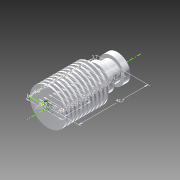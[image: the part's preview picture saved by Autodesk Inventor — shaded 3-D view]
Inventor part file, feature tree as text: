
AUTODESK INVENTOR PART (.ipt)
format: ipt  version: 2015 (Build 190159000, 159)  size: 478,720 bytes
history: native  units: mm
features: sketch x3, hole x3, other x2, revolve x1
ambient origin geometry x8: Origin, YZ Plane, XZ Plane, XY Plane, X Axis, Y Axis, Z Axis, Center Point
bodies: Body1 (feature_tree)
feature tree (9):
  other  "Твердое тело1"
  sketch  "Эскиз1"
  revolve  "Вращение1"
  sketch  "Эскиз2"
  hole  "Отверстие1"  [1 undecoded]
  hole  "Отверстие3"  [1 undecoded]
  hole  "Отверстие4"  [1 undecoded]
  other  "Пружина3"
  sketch  "Эскиз3"
note: 3 required parameter values undecoded (feature->parameter linkage not recoverable at this tier; creation-order binding heuristic only, values carry confidence <= 0.55)
